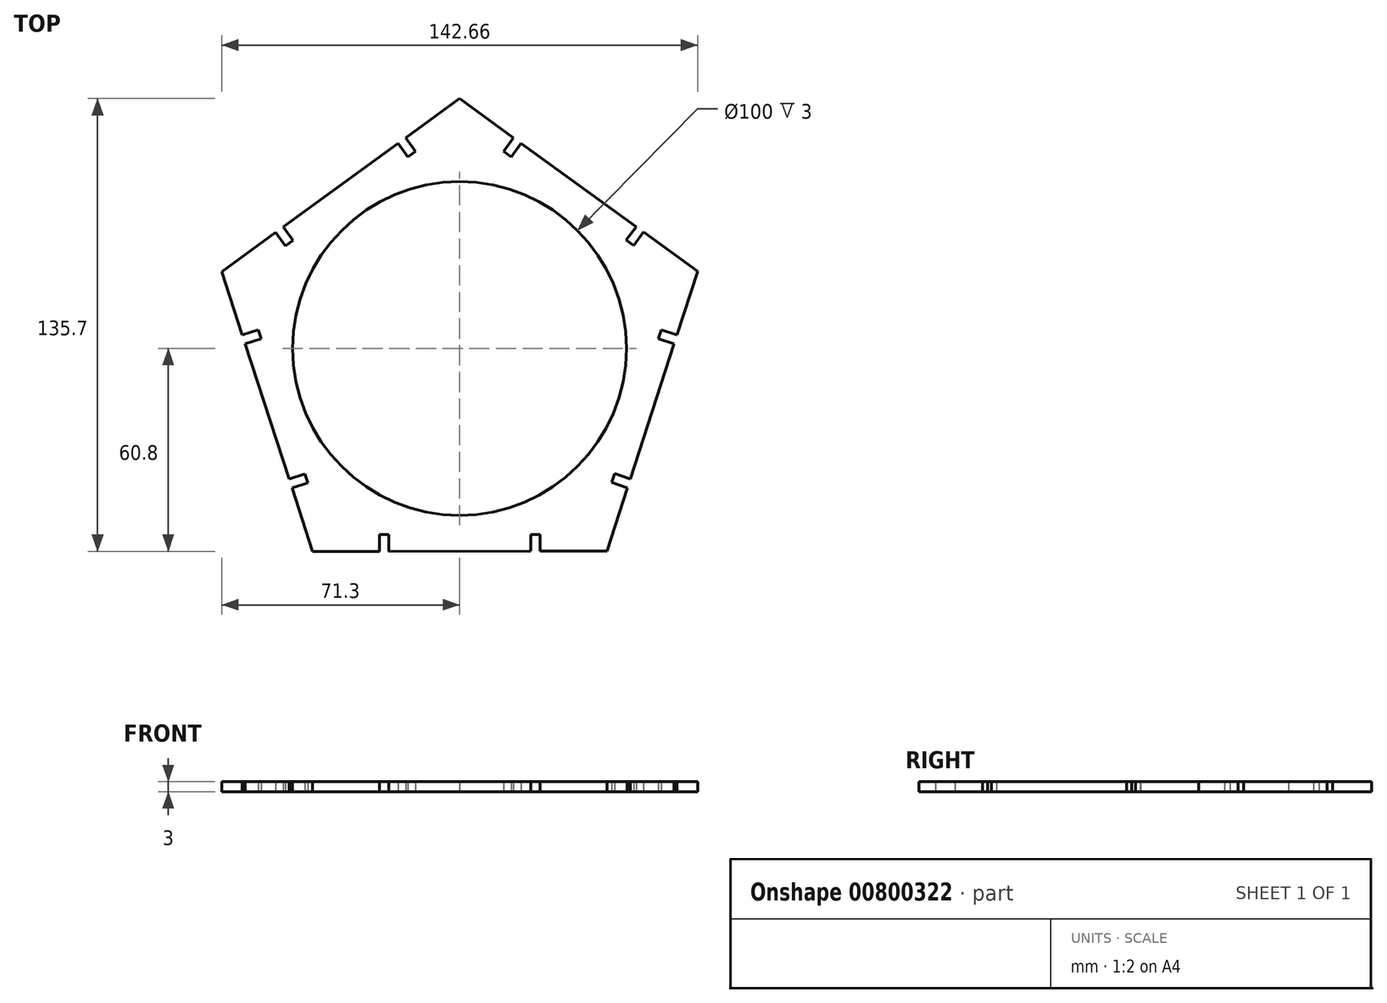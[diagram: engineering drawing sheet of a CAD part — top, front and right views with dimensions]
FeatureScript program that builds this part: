
annotation { "Feature Type Name" : "Feature", "Feature Type Description" : "" }
export const myFeature = defineFeature(function(context is Context, id is Id, definition is map)
    precondition{}
    {
        {
            var Q0;
            Q0=qCreatedBy(makeId("Top.planeOp"),FACE);
            var sketch = newSketch(context, id + "F0", { "sketchPlane" : qUnion([Q0])});
            skCircle(sketch, "E0.cCircle", {"center": v(0.04, -0.1) * mm, "radius": 75 * mm, "construction": true});
            skLineSegment(sketch, "E0.0", {"start": v(0, 74.9) * mm, "end": v(16.19, 63.15) * mm});
            skLineSegment(sketch, "E0.1", {"start": v(71.36, 23.11) * mm, "end": v(65.19, 4.1) * mm});
            skLineSegment(sketch, "E0.2", {"start": v(44.16, -60.75) * mm, "end": v(24.16, -60.76) * mm});
            skLineSegment(sketch, "E0.3", {"start": v(-44.01, -60.8) * mm, "end": v(-50.2, -41.78) * mm});
            skLineSegment(sketch, "E0.4", {"start": v(-71.3, 23.04) * mm, "end": v(-55.13, 34.8) * mm});
            skLineSegment(sketch, "E1", {"start": v(-16.17, 63.14) * mm, "end": v(-13.23, 59.1) * mm});
            skLineSegment(sketch, "E2", {"start": v(-13.23, 59.1) * mm, "end": v(-15.5, 57.44) * mm});
            skLineSegment(sketch, "E3", {"start": v(-15.5, 57.44) * mm, "end": v(-18.44, 61.49) * mm});
            skLineSegment(sketch, "E4.trimOffspring", {"start": v(-16.17, 63.14) * mm, "end": v(0, 74.9) * mm});
            skLineSegment(sketch, "E5.MirrorCS", {"start": v(-55.13, 34.8) * mm, "end": v(-52.19, 30.76) * mm});
            skLineSegment(sketch, "E6.MirrorCS", {"start": v(-49.92, 32.4) * mm, "end": v(-52.86, 36.45) * mm});
            skLineSegment(sketch, "E7.MirrorCS", {"start": v(-52.19, 30.76) * mm, "end": v(-49.92, 32.4) * mm});
            skLineSegment(sketch, "E8.trimOffspring", {"start": v(-52.86, 36.45) * mm, "end": v(-18.44, 61.49) * mm});
            skLineSegment(sketch, "E9.1.0", {"start": v(-65.11, 4.02) * mm, "end": v(-60.36, 5.57) * mm});
            skLineSegment(sketch, "E9.1.1", {"start": v(-59.49, 2.9) * mm, "end": v(-64.24, 1.36) * mm});
            skLineSegment(sketch, "E9.1.2", {"start": v(-60.36, 5.57) * mm, "end": v(-59.49, 2.9) * mm});
            skLineSegment(sketch, "E9.1.3", {"start": v(-46.31, -37.57) * mm, "end": v(-51.07, -39.12) * mm});
            skLineSegment(sketch, "E9.1.4", {"start": v(-45.45, -40.23) * mm, "end": v(-46.31, -37.57) * mm});
            skLineSegment(sketch, "E9.1.5", {"start": v(-50.2, -41.78) * mm, "end": v(-45.45, -40.23) * mm});
            skLineSegment(sketch, "E9.2.0", {"start": v(-24.01, -60.79) * mm, "end": v(-24.01, -55.79) * mm});
            skLineSegment(sketch, "E9.2.1", {"start": v(-21.21, -55.79) * mm, "end": v(-21.21, -60.79) * mm});
            skLineSegment(sketch, "E9.2.2", {"start": v(-24.01, -55.79) * mm, "end": v(-21.21, -55.79) * mm});
            skLineSegment(sketch, "E9.2.3", {"start": v(21.35, -55.76) * mm, "end": v(21.36, -60.76) * mm});
            skLineSegment(sketch, "E9.2.4", {"start": v(24.15, -55.76) * mm, "end": v(21.35, -55.76) * mm});
            skLineSegment(sketch, "E9.2.5", {"start": v(24.16, -60.76) * mm, "end": v(24.15, -55.76) * mm});
            skLineSegment(sketch, "E9.3.0", {"start": v(50.33, -41.73) * mm, "end": v(45.57, -40.19) * mm});
            skLineSegment(sketch, "E9.3.1", {"start": v(46.43, -37.52) * mm, "end": v(51.2, -39.06) * mm});
            skLineSegment(sketch, "E9.3.3", {"start": v(59.57, 2.97) * mm, "end": v(64.32, 1.43) * mm});
            skLineSegment(sketch, "E9.3.4", {"start": v(60.43, 5.63) * mm, "end": v(59.57, 2.97) * mm});
            skLineSegment(sketch, "E9.3.5", {"start": v(65.19, 4.1) * mm, "end": v(60.43, 5.63) * mm});
            skLineSegment(sketch, "E9.4.0", {"start": v(55.17, 34.86) * mm, "end": v(52.23, 30.81) * mm});
            skLineSegment(sketch, "E9.4.1", {"start": v(49.97, 32.46) * mm, "end": v(52.9, 36.5) * mm});
            skLineSegment(sketch, "E9.4.2", {"start": v(52.23, 30.81) * mm, "end": v(49.97, 32.46) * mm});
            skLineSegment(sketch, "E9.4.3", {"start": v(15.52, 57.46) * mm, "end": v(18.45, 61.5) * mm});
            skLineSegment(sketch, "E9.4.4", {"start": v(13.25, 59.1) * mm, "end": v(15.52, 57.46) * mm});
            skLineSegment(sketch, "E9.4.5", {"start": v(16.19, 63.15) * mm, "end": v(13.25, 59.1) * mm});
            skLineSegment(sketch, "E10.trimOffspring", {"start": v(-65.11, 4.02) * mm, "end": v(-71.3, 23.04) * mm});
            skLineSegment(sketch, "E11.trimOffspring", {"start": v(21.36, -60.76) * mm, "end": v(-21.21, -60.79) * mm});
            skLineSegment(sketch, "E12.trimOffspring", {"start": v(-24.01, -60.79) * mm, "end": v(-44.01, -60.8) * mm});
            skLineSegment(sketch, "E13.trimOffspring", {"start": v(-51.07, -39.12) * mm, "end": v(-64.24, 1.36) * mm});
            skLineSegment(sketch, "E14.trimOffspring", {"start": v(18.45, 61.5) * mm, "end": v(52.9, 36.5) * mm});
            skLineSegment(sketch, "E15.trimOffspring", {"start": v(55.17, 34.86) * mm, "end": v(71.36, 23.11) * mm});
            skLineSegment(sketch, "E16.trimOffspring", {"start": v(64.32, 1.43) * mm, "end": v(51.2, -39.06) * mm});
            skLineSegment(sketch, "E17.trimOffspring", {"start": v(50.33, -41.73) * mm, "end": v(44.16, -60.75) * mm});
            skCircle(sketch, "E18.cCircle", {"center": v(0.04, -0.1) * mm, "radius": 60 * mm, "construction": true});
            skPoint(sketch, "E19.0.midPoint", {"position": v(-25.66, -36.97) * mm});
            skLineSegment(sketch, "E20", {"start": v(46.43, -37.52) * mm, "end": v(45.57, -40.19) * mm});
            skPoint(sketch, "E21.0.midPoint", {"position": v(7.75, -34.24) * mm});
            skCircle(sketch, "E22", {"center": v(0, 0) * mm, "radius": 50 * mm});
            skSolve(sketch);
        }
        {
            var Q0;
            Q0=qSketchRegion(id+"F0",true);
            extrude(context, id + "F1", {"entities" : qUnion([Q0]), "depth" : 3 * mm, "offsetDistance" : 25 * mm});
        }
    });
